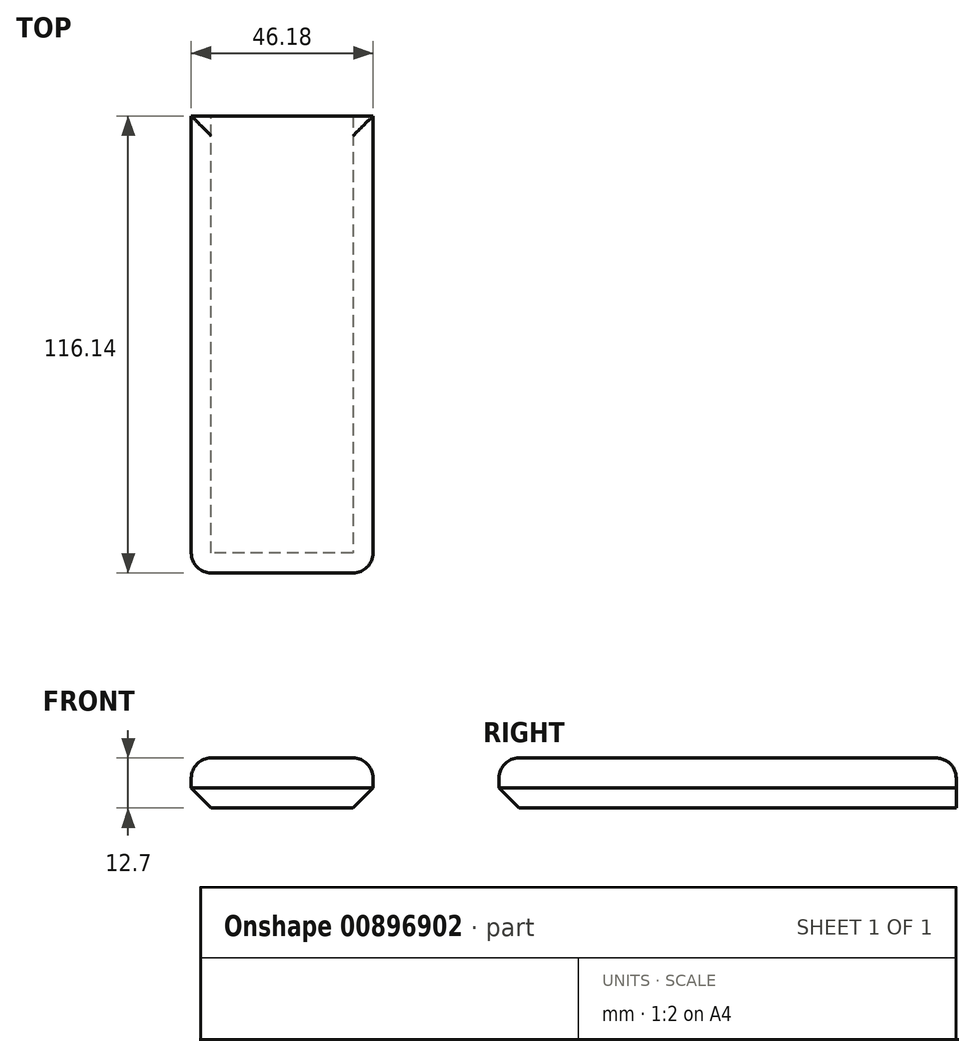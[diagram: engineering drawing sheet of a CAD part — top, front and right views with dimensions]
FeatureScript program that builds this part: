
annotation { "Feature Type Name" : "Feature", "Feature Type Description" : "" }
export const myFeature = defineFeature(function(context is Context, id is Id, definition is map)
    precondition{}
    {
        {
            var Q0;
            Q0=qCreatedBy(makeId("Top.planeOp"),FACE);
            var sketch = newSketch(context, id + "F0", { "sketchPlane" : qUnion([Q0])});
            skLineSegment(sketch, "E0.bottom", {"start": v(-23.09, 58.07) * mm, "end": v(23.09, 58.07) * mm});
            skLineSegment(sketch, "E0.top", {"start": v(-23.09, -58.07) * mm, "end": v(23.09, -58.07) * mm});
            skLineSegment(sketch, "E0.left", {"start": v(-23.09, 58.07) * mm, "end": v(-23.09, -58.07) * mm});
            skLineSegment(sketch, "E0.right", {"start": v(23.09, 58.07) * mm, "end": v(23.09, -58.07) * mm});
            skPoint(sketch, "E0.middle", {"position": v(0, 0) * mm});
            skSolve(sketch);
        }
        {
            var Q0;
            Q0=makeQuery(id+"F0.imprint","IMPRINT",FACE,{"disambiguationData":[TD([[makeQuery(id+"F0.imprint","IMPRINT",EDGE,{"derivedFrom":sQuery(id+"F0.wireOp",EDGE,"E0.bottom")}),-1.0]])]});
            extrude(context, id + "F1", {"entities" : qUnion([Q0]), "depth" : 12.7 * mm, "offsetDistance" : 25.4 * mm});
        }
        {
            var Q0;
            Q0=makeQuery(id+"F1.opExtrude","CAP_EDGE",EDGE,{"disambiguationData":[OSD([sQuery(id+"F0.wireOp",EDGE,"E0.top")])],"isStart":false});
            fillet(context, id + "F2", {"entities" : qUnion([Q0]), "radius" : 5.08 * mm, "tangentPropagation" : true, "allowEdgeOverflow" : false});
        }
        {
            var Q0;
            Q0=makeQuery(id+"F1.opExtrude","CAP_EDGE",EDGE,{"disambiguationData":[OSD([sQuery(id+"F0.wireOp",EDGE,"E0.right")])],"isStart":false});
            var Q1;
            Q1=makeQuery(id+"F1.opExtrude","CAP_EDGE",EDGE,{"disambiguationData":[OSD([sQuery(id+"F0.wireOp",EDGE,"E0.left")])],"isStart":false});
            var Q2;
            Q2=makeQuery(id+"F1.opExtrude","CAP_EDGE",EDGE,{"disambiguationData":[OSD([sQuery(id+"F0.wireOp",EDGE,"E0.bottom")])],"isStart":false});
            fillet(context, id + "F3", {"entities" : qUnion([Q0, Q1, Q2]), "radius" : 5.08 * mm, "tangentPropagation" : true, "allowEdgeOverflow" : false});
        }
        {
            var Q0;
            Q0=makeQuery(id+"F1.opExtrude","CAP_EDGE",EDGE,{"disambiguationData":[OSD([sQuery(id+"F0.wireOp",EDGE,"E0.top")])],"isStart":true});
            chamfer(context, id + "F4", {"entities" : qUnion([Q0]), "width" : 5.08 * mm, "tangentPropagation" : true});
        }
    });
